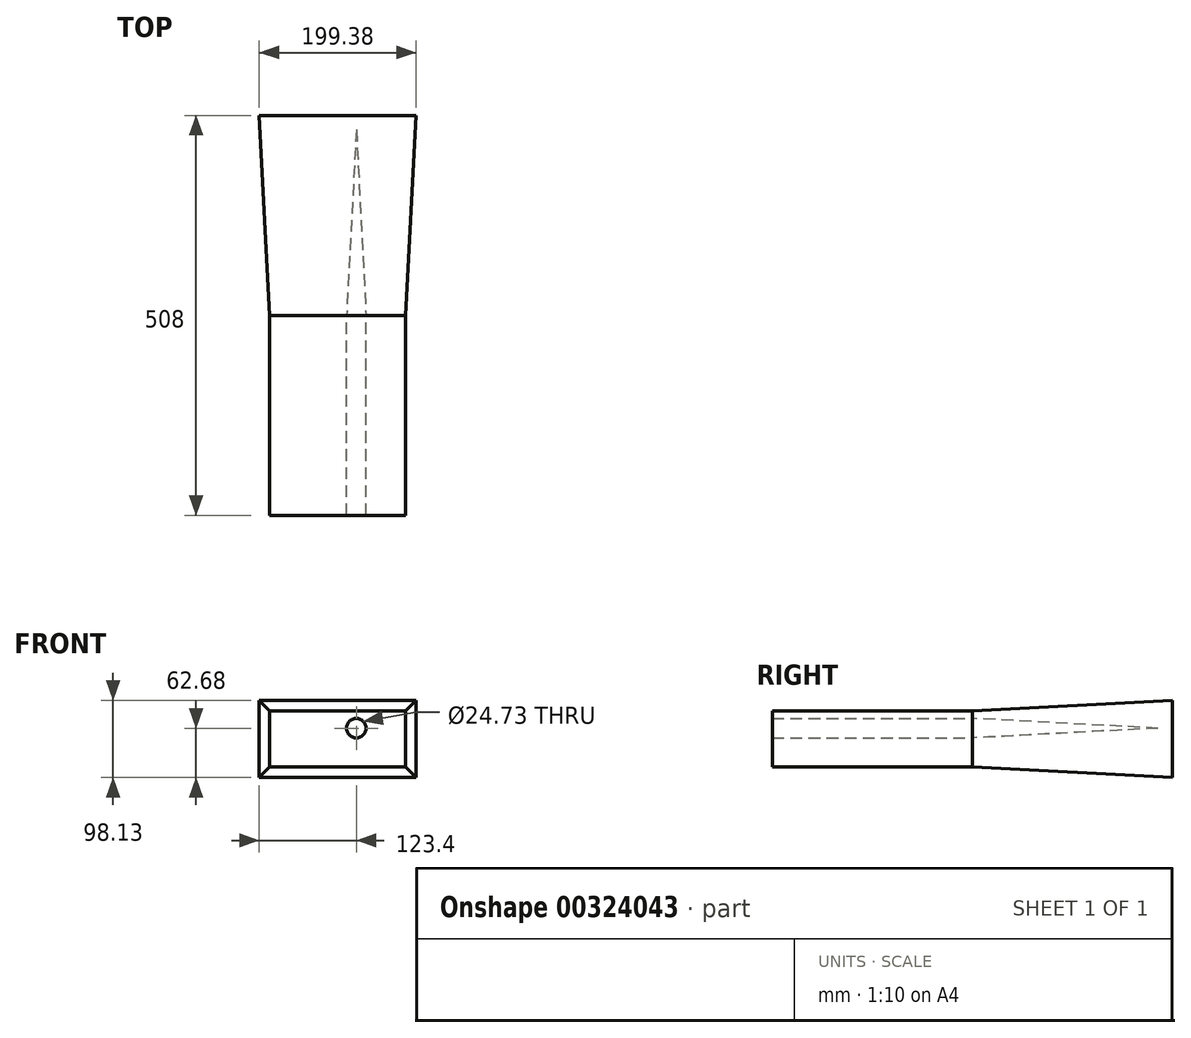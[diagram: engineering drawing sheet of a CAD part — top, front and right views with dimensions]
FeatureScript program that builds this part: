
annotation { "Feature Type Name" : "Feature", "Feature Type Description" : "" }
export const myFeature = defineFeature(function(context is Context, id is Id, definition is map)
    precondition{}
    {
        {
            var Q0;
            Q0=qCreatedBy(makeId("Front.planeOp"),FACE);
            var sketch = newSketch(context, id + "F0", { "sketchPlane" : qUnion([Q0])});
            skLineSegment(sketch, "E0.bottom", {"start": v(-110.09, 22.13) * mm, "end": v(62.66, 22.13) * mm});
            skLineSegment(sketch, "E0.top", {"start": v(-110.09, -49.37) * mm, "end": v(62.66, -49.37) * mm});
            skLineSegment(sketch, "E0.left", {"start": v(-110.09, 22.13) * mm, "end": v(-110.09, -49.37) * mm});
            skLineSegment(sketch, "E0.right", {"start": v(62.66, 22.13) * mm, "end": v(62.66, -49.37) * mm});
            skCircle(sketch, "E1", {"center": v(0, 0) * mm, "radius": 12.37 * mm});
            skSolve(sketch);
        }
        {
            var Q0;
            Q0 = qSketchRegion(id + "F0", true);
            extrude(context, id + "F1", {"entities" : qUnion([Q0]), "depth" : 254 * mm, "hasSecondDirection" : true, "secondDirectionOppositeDirection" : true, "secondDirectionDepth" : 254 * mm, "hasSecondDirectionDraft" : true, "secondDirectionDraftAngle" : 3 * degree});
        }
    });
